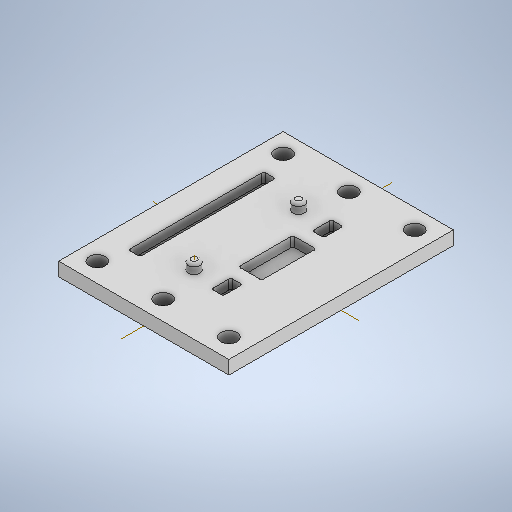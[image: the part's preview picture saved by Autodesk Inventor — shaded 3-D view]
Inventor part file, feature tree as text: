
AUTODESK INVENTOR PART (.ipt)
format: ipt  version: 2025 (Build 290162000, 162)  size: 329,216 bytes
history: native  units: mm
features: sketch x6, extrude x5, mirror x2, fillet x2, hole x1, pattern_linear x1, other x1
ambient origin geometry x8: Origin, YZ Plane, XZ Plane, XY Plane, X Axis, Y Axis, Z Axis, Center Point
bodies: Solid1 (feature_tree)
feature tree (18):
  extrude  "Extrusion1"  Depth=58.0mm
  hole  "Hole1"  [1 undecoded]
  pattern_linear  "Rectangular Pattern1"  Count1=2 Spacing1=17.0mm
  mirror  "Mirror1"
  extrude  "Extrusion2"  Depth=3.0mm
  fillet  "Fillet1"  Radius=2.5mm
  extrude  "Extrusion3"  Depth=2.5mm TaperAngle=0.0deg
  other  "Work Axis1"
  extrude  "Extrusion4"  Depth=2.5mm
  extrude  "Extrusion5"  Depth=3.0mm
  mirror  "Mirror2"
  fillet  "Fillet2"  Radius=35.0mm
  sketch  "Sketch1"  dims[d2=44.0mm d3=58.0mm]
  sketch  "Sketch2"  dims[d13=3.5mm d14=0.0mm]
  sketch  "Sketch3"  dims[d15=4.2mm d16=6.0mm d17=4.0mm d18=2.0mm d19=90.0deg d20=8.0mm d21=20.594885mm d22=5.0mm d23=20.0mm d25=17.0mm]
  sketch  "Sketch4"  dims[d26=20.0mm d28=17.0mm d29=3.0mm d30=2.5mm]
  sketch  "Sketch5"  dims[d31=13.5mm d32=2.5mm d33=0.0mm]
  sketch  "Sketch6"  dims[d34=0.75mm d35=2.5mm d36=3.0mm d37=35.0mm d38=0.0mm d39=14.0mm d40=6.0mm d41=2.5mm d42=8.0mm d43=14.0mm d44=0.0mm d45=3.0mm d46=5.0mm d47=3.0mm d48=3.5mm d49=2.5mm d50=0.0mm d51=0.5mm]
note: 1 required parameter value undecoded (feature->parameter linkage not recoverable at this tier; creation-order binding heuristic only, values carry confidence <= 0.55)
